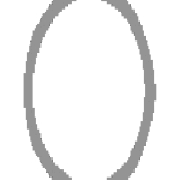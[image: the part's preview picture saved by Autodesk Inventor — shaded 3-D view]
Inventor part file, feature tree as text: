
AUTODESK INVENTOR PART (.ipt)
format: ipt  version: 2021 (Build 250183000, 183)  size: 113,152 bytes
history: native  units: in
note: dims shown in document units (in); Inventor stores cm internally (conversion verified against a paired STEP export)
features: other x4, sketch x3, plane x1
ambient origin geometry x8: Origin, YZ Plane, XZ Plane, XY Plane, X Axis, Y Axis, Z Axis, Center Point
bodies: Solid1 (feature_tree), Body (feature_tree)
feature tree (8):
  other  "Driven Length"
  other  "Frame Generator"
  other  "Start Plane"
  other  "End Plane"
  sketch  "Sketch"  dims[d2=14.625in d4=-0.0in d5=14.625in d6=0.12in d7=0.0in d8=90.0deg d9=14.625in]
  sketch  "Sketch2"  dims[d0=1.0in]
  plane  "Work Plane3"
  sketch  "Sketch3"  dims[d1=0.065in]
